# Revit family: Bticino-Door Entry System-IP-Entrance Panel
name_source: partatom
category: Equipement électrique
units: mm (PartAtom-declared; Revit-internal decimal feet)

## family parameters
Configuration du panneau = Deux colonnes, circuits au sein
Cote de connecteur circulaire = Utiliser le diamètre
Couper avec des vides une fois chargée = Non
Hôte = Face
Partagée = Non
Point de calcul de pièce = Non
Type d'élément = Tableau de raccordement

## types (6) — shared parameters
Color = Black
Configurator website = https://www.homesystems-legrandgroup.com
Connection type = RJ45 Cable
Elévation par défaut = 1100 mm
Fabricant = BTICINO
General Conditions of Use = https://export.legrand.com
IK = 07
IP = 54
Installation method = Flush-mounting
Interface type = Network technology
Operating temperature MIN-MAX = -40/+70 °C
Tension = 24 V DC

## per-type parameters (varying)
| type | Built-in depth | Camera | Height | Modélisation | Product designation | Recessed height | Recessed width | Reference | Touchscreen | Width | With fingerprint |
| ENTRANCE PANEL FULL 10" | 60 mm  [stored 0.19685 ft] | With Camera | 430 mm  [stored 1.41076 ft] | Panel 10'' : 374000 | IP - ENTRANCE PANEL FULL 10" - FINGERPRINT | 415 mm  [stored 1.36155 ft] | 184 mm  [stored 0.603675 ft] | BT-374000 | Oui | 195 mm  [stored 0.639764 ft] | Oui |
| ENTRANCE PANEL 10" | 60 mm  [stored 0.19685 ft] | With Camera | 430 mm  [stored 1.41076 ft] | Panel 10'' : 374002 | IP - ENTRANCE PANEL 10" | 415 mm  [stored 1.36155 ft] | 184 mm  [stored 0.603675 ft] | BT-374002 | Oui | 195 mm  [stored 0.639764 ft] | Non |
| ENTRANCE PANEL KEYPAD FULL | 60 mm  [stored 0.19685 ft] | With Camera | 400 mm  [stored 1.31234 ft] | Panel keypad' : 374001 | IP - ENTRANCE PANEL KEYPAD FULL - FINGERPRINT | 384 mm  [stored 1.25984 ft] | 149 mm  [stored 0.488845 ft] | BT-374001 | Non | 160 mm  [stored 0.524934 ft] | Oui |
| ENTRANCE PANEL KEYPAD | 60 mm  [stored 0.19685 ft] | Without camera | 400 mm  [stored 1.31234 ft] | Panel keypad' : 374003 | IP - ENTRANCE PANEL KEYPAD | 384 mm  [stored 1.25984 ft] | 149 mm  [stored 0.488845 ft] | BT-374003 | Non | 160 mm  [stored 0.524934 ft] | Non |
| SMALL ENTRANCE PANEL 4.3" TOUCH DISPLAY | 62 mm  [stored 0.203412 ft] | With night vision camera | 245 mm  [stored 0.803806 ft] | Small panel Touch display : 374005 | IP - SMALL ENTRANCE PANEL 4.3" TOUCH DISPLAY | 232 mm  [stored 0.761155 ft] | 82 mm  [stored 0.269029 ft] | BT-374005 | Oui | 92 mm  [stored 0.301837 ft] | Non |
| SMALL ENTRANCE PANEL | 59 mm | With Camera | 193 mm  [stored 0.633202 ft] | Small panel : 374004 | IP - SMALL ENTRANCE PANEL | 178 mm  [stored 0.58399 ft] | 84 mm  [stored 0.275591 ft] | BT-374004 | Non | 94 mm  [stored 0.308399 ft] | Non |

note: [stored X ft] marks values corroborated as IEEE doubles in the binary element streams (Revit-internal decimal feet)
